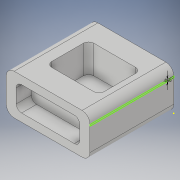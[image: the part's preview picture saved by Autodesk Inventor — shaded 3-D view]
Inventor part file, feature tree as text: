
AUTODESK INVENTOR PART (.ipt)
format: ipt  version: 2017 (Build 210142000, 142)  size: 166,400 bytes
history: native  units: in
note: dims shown in document units (in); Inventor stores cm internally (conversion verified against a paired STEP export)
features: sketch x5, extrude x4
ambient origin geometry x8: Origin, YZ Plane, XZ Plane, XY Plane, X Axis, Y Axis, Z Axis, Center Point
bodies: Solid1 (feature_tree)
feature tree (9):
  extrude  "Extrusion1"  Depth=1.53in
  extrude  "Extrusion2"  Depth=0.3in
  extrude  "Extrusion3"  Depth=0.3in
  extrude  "Extrusion4"  Depth=2.4in
  sketch  "Sketch5"  dims[d13=0.93in d16=0.2in d17=0.57in d18=0.0in d19=1.59in d20=1.98in d21=0.5in d22=1.07in d23=0.0in d26=1.0in d27=2.5in d29=1.0in d30=0.2in d31=0.57in d32=0.0in d33=0.2in d34=0.06in]
  sketch  "Sketch1"  dims[d2=3.17in d3=1.53in]
  sketch  "Sketch2"  dims[d4=0.3in d5=0.3in]
  sketch  "Sketch3"  dims[d6=0.3in d7=0.3in]
  sketch  "Sketch4"  dims[d10=3.17in d11=0.0in d12=2.4in]
